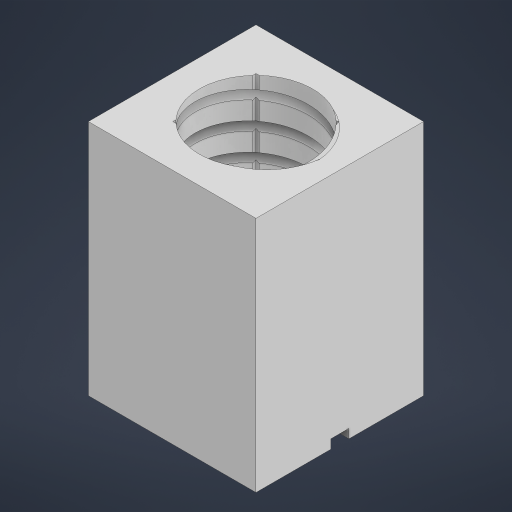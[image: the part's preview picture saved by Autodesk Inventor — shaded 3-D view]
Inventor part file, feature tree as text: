
AUTODESK INVENTOR PART (.ipt)
format: ipt  version: 2024.1 (Build 281209000, 209)  size: 1,145,344 bytes
history: native  units: mm
features: sketch x6, projected_geometry x6, extrude x5, helix x1
ambient origin geometry x8: Origin, YZ Plane, XZ Plane, XY Plane, X Axis, Y Axis, Z Axis, Center Point
bodies: Solid1 (feature_tree)
feature tree (18):
  extrude  "Extrusion1"  Depth=15.0mm
  extrude  "Extrusion2"  Depth=2.0mm TaperAngle=0.0deg
  extrude  "Extrusion3"  Depth=18.36mm
  helix  "Coil1"  [1 undecoded]
  extrude  "Extrusion4"  Depth=50.0mm TaperAngle=0.0deg
  extrude  "Extrusion5"  Depth=2.5mm
  sketch  "Sketch1"  dims[d0=15.0mm d1=15.0mm]
  sketch  "Sketch2"  dims[d2=37.0mm d3=2.0mm d4=0.0mm]
  projected_geometry  "Projected Loop1"
  sketch  "Sketch3"  dims[d6=18.36mm d7=18.36mm d8=0.4mm d9=0.0mm]
  projected_geometry  "Projected Loop2"
  sketch  "Sketch4"  dims[d10=25.0mm d11=50.0mm d12=0.0mm]
  sketch  "Sketch5"  dims[d13=60.0deg d14=2.5mm]
  projected_geometry  "Projected Loop3"
  projected_geometry  "Projected Loop4"
  projected_geometry  "Projected Loop5"
  projected_geometry  "Projected Loop6"
  sketch  "Sketch6"  dims[d15=2.0mm d16=6.0mm d17=10.0mm d18=100.0mm d19=0.0mm d20=90.0deg d21=90.0deg d22=0.0mm d23=0.0mm d24=21.0mm d25=50.0mm d26=0.0mm d27=4.0mm d28=10.0mm d29=0.0mm]
note: 1 required parameter value undecoded (feature->parameter linkage not recoverable at this tier; creation-order binding heuristic only, values carry confidence <= 0.55)
